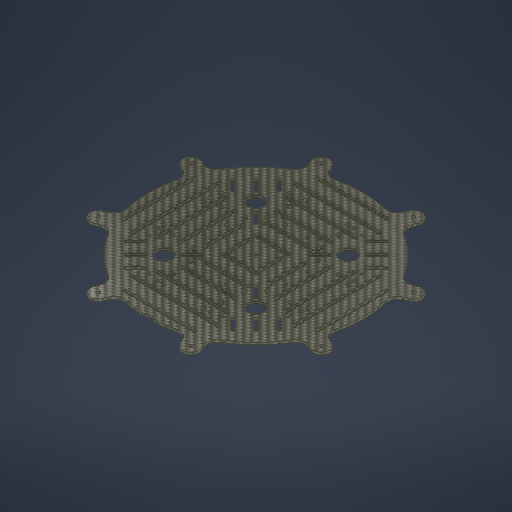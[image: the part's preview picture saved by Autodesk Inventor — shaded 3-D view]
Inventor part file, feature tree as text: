
AUTODESK INVENTOR PART (.ipt)
format: ipt  version: 2025 (Build 290162010, 162A)  size: 921,600 bytes
history: native  units: mm
features: extrude x1, sketch x1
ambient origin geometry x8: Origin, YZ Plane, XZ Plane, XY Plane, X Axis, Y Axis, Z Axis, Center Point
bodies: Solid1 (feature_tree)
feature tree (2):
  extrude  "Extrusion1"  [1 undecoded]
  sketch  "Sketch1"  dims[d0=2.0mm d1=0.0mm]
note: 1 required parameter value undecoded (feature->parameter linkage not recoverable at this tier; creation-order binding heuristic only, values carry confidence <= 0.55)
